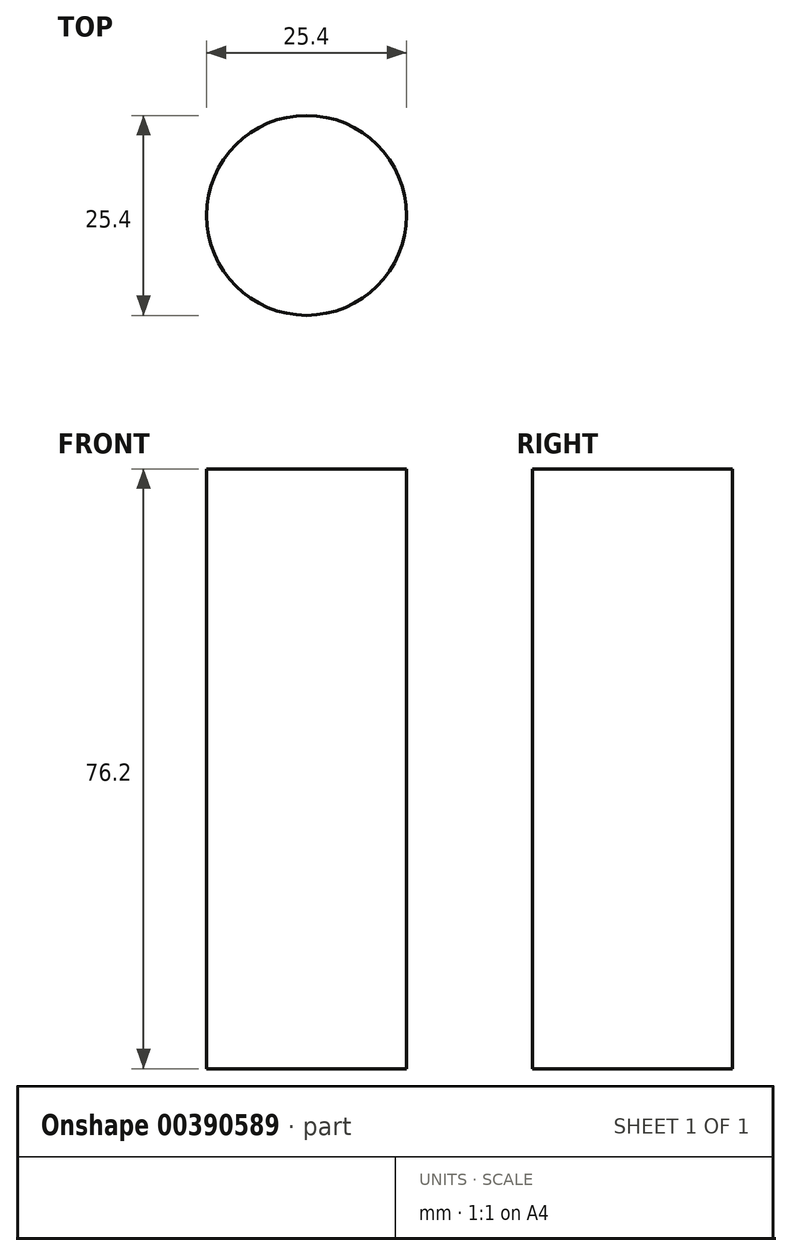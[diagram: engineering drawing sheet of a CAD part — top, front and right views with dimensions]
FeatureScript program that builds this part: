
annotation { "Feature Type Name" : "Feature", "Feature Type Description" : "" }
export const myFeature = defineFeature(function(context is Context, id is Id, definition is map)
    precondition{}
    {
        {
            var Q0;
            Q0=qCreatedBy(makeId("Top.planeOp"),FACE);
            var sketch = newSketch(context, id + "F0", { "sketchPlane" : qUnion([Q0])});
            skCircle(sketch, "E0", {"center": v(0, 0) * mm, "radius": 12.7 * mm});
            skSolve(sketch);
        }
        {
            var Q0;
            Q0 = qSketchRegion(id + "F0", true);
            extrude(context, id + "F1", {"entities" : qUnion([Q0]), "depth" : 76.2 * mm});
        }
    });
